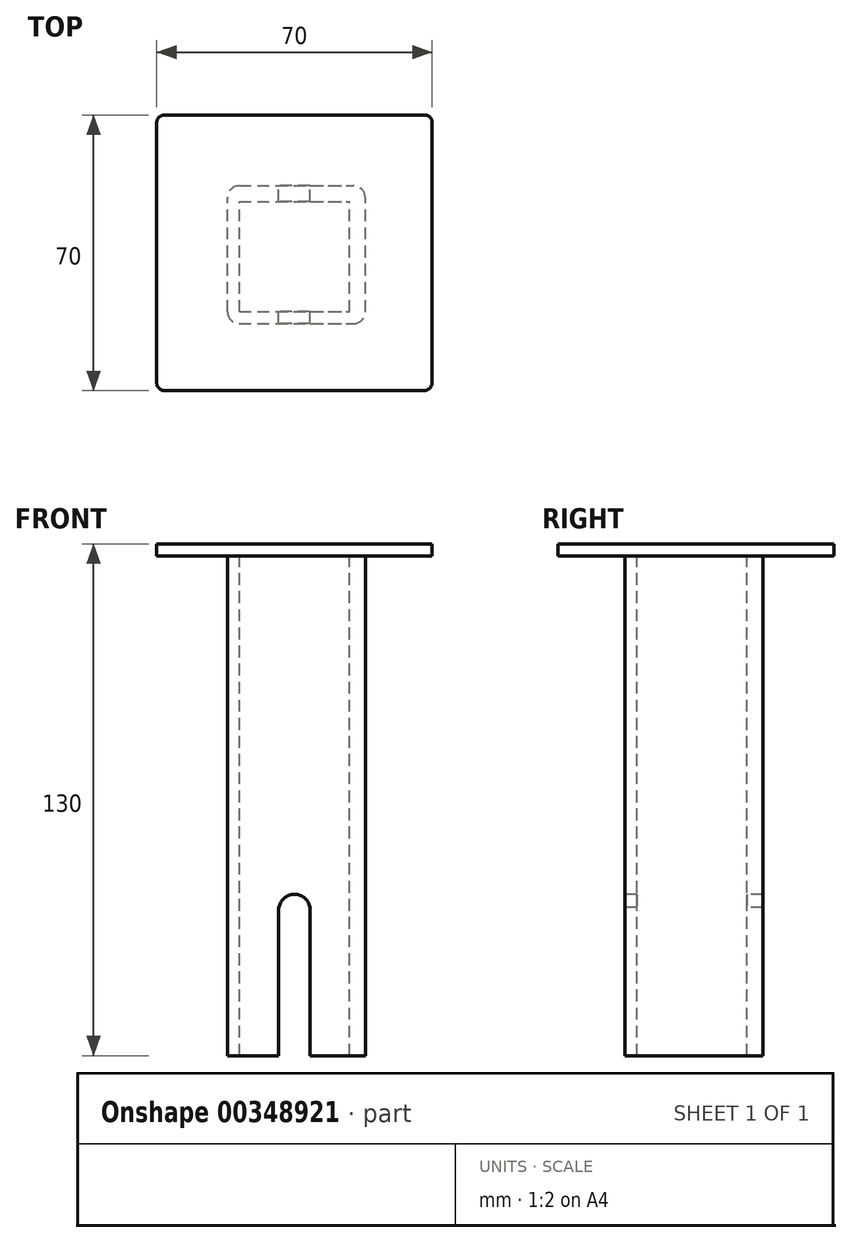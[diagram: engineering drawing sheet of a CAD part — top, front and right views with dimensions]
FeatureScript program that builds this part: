
annotation { "Feature Type Name" : "Feature", "Feature Type Description" : "" }
export const myFeature = defineFeature(function(context is Context, id is Id, definition is map)
    precondition{}
    {
        {
            var Q0;
            Q0=qCreatedBy(makeId("Top.planeOp"),FACE);
            var sketch = newSketch(context, id + "F0", { "sketchPlane" : qUnion([Q0])});
            skLineSegment(sketch, "E0.bottom", {"start": v(-35.5, -38.08) * mm, "end": v(34.5, -38.08) * mm});
            skLineSegment(sketch, "E0.top", {"start": v(-35.5, 31.92) * mm, "end": v(34.5, 31.92) * mm});
            skLineSegment(sketch, "E0.left", {"start": v(-35.5, -38.08) * mm, "end": v(-35.5, 31.92) * mm});
            skLineSegment(sketch, "E0.right", {"start": v(34.5, -38.08) * mm, "end": v(34.5, 31.92) * mm});
            skLineSegment(sketch, "E1", {"start": v(-35.5, -3.08) * mm, "end": v(-17.5, -3.08) * mm, "construction": true});
            skPoint(sketch, "E1.endSnap0", {"position": v(-35.5, -3.08) * mm});
            skLineSegment(sketch, "E2.bottom", {"start": v(-17.5, -21.08) * mm, "end": v(17.5, -21.08) * mm});
            skLineSegment(sketch, "E2.top", {"start": v(-17.5, 13.92) * mm, "end": v(17.5, 13.92) * mm});
            skLineSegment(sketch, "E2.left", {"start": v(-17.5, -21.08) * mm, "end": v(-17.5, 13.92) * mm});
            skLineSegment(sketch, "E2.right", {"start": v(17.5, -21.08) * mm, "end": v(17.5, 13.92) * mm});
            skLineSegment(sketch, "E3", {"start": v(-0.5, 31.92) * mm, "end": v(-0.5, 13.92) * mm, "construction": true});
            skPoint(sketch, "E3.endSnap0", {"position": v(0, 13.92) * mm});
            skLineSegment(sketch, "E4", {"start": v(-17.5, -3.08) * mm, "end": v(-14.5, -3.08) * mm, "construction": true});
            skLineSegment(sketch, "E5.bottom", {"start": v(-14.5, -18.08) * mm, "end": v(13.5, -18.08) * mm});
            skLineSegment(sketch, "E5.top", {"start": v(-14.5, 9.92) * mm, "end": v(13.5, 9.92) * mm});
            skLineSegment(sketch, "E5.left", {"start": v(-14.5, -18.08) * mm, "end": v(-14.5, 9.92) * mm});
            skLineSegment(sketch, "E5.right", {"start": v(13.5, -18.08) * mm, "end": v(13.5, 9.92) * mm});
            skLineSegment(sketch, "E6", {"start": v(0, -21.08) * mm, "end": v(0, -18.08) * mm, "construction": true});
            skLineSegment(sketch, "E7", {"start": v(-35.5, -38.08) * mm, "end": v(34.5, 31.92) * mm, "construction": true});
            skLineSegment(sketch, "E8", {"start": v(0, -21.08) * mm, "end": v(0, -38.08) * mm, "construction": true});
            skSolve(sketch);
        }
        {
            var Q0;
            {var subQ1=sQuery(id+"F0.wireOp",EDGE,"E0.bottom");Q0=makeQuery(id+"F0.imprint","IMPRINT",FACE,{"disambiguationData":[TD([[makeQuery(id+"F0.imprint","IMPRINT",EDGE,{"derivedFrom":subQ1}),1.0]])]});}
            var Q1;
            {var subQ7=sQuery(id+"F0.wireOp",EDGE,"E1");Q1=makeQuery(id+"F0.imprint","IMPRINT",FACE,{"disambiguationData":[TD([[makeQuery(id+"F0.imprint","IMPRINT",EDGE,{"derivedFrom":subQ7}),1.0]])]});}
            var Q2;
            {var subQ3=sQuery(id+"F0.wireOp",EDGE,"E5.bottom");Q2=makeQuery(id+"F0.imprint","IMPRINT",FACE,{"disambiguationData":[TD([[makeQuery(id+"F0.imprint","IMPRINT",EDGE,{"derivedFrom":subQ3}),1.0]])]});}
            var Q3;
            {var subQ9=sQuery(id+"F0.wireOp",EDGE,"E2.bottom");Q3=makeQuery(id+"F0.imprint","IMPRINT",FACE,{"disambiguationData":[TD([[makeQuery(id+"F0.imprint","IMPRINT",EDGE,{"derivedFrom":subQ9}),1.0]])]});}
            extrude(context, id + "F1", {"entities" : qUnion([Q0, Q1, Q2, Q3]), "oppositeDirection" : true, "depth" : 3 * mm});
        }
        {
            var Q0;
            {var subQ9=sQuery(id+"F0.wireOp",EDGE,"E2.bottom");Q0=makeQuery(id+"F0.imprint","IMPRINT",FACE,{"disambiguationData":[TD([[makeQuery(id+"F0.imprint","IMPRINT",EDGE,{"derivedFrom":subQ9}),1.0]])]});}
            extrude(context, id + "F2", {"entities" : qUnion([Q0]), "operationType" : NewBodyOperationType.ADD, "oppositeDirection" : true, "depth" : 130 * mm});
        }
        {
            var Q0;
            Q0=makeQuery(id+"F1.opExtrude","SWEPT_EDGE",EDGE,{"disambiguationData":[OSD([sQuery(id+"F0.wireOp",EDGE,"E0.bottom"),sQuery(id+"F0.wireOp",EDGE,"E0.left")])]});
            var Q1;
            Q1=makeQuery(id+"F1.opExtrude","SWEPT_EDGE",EDGE,{"disambiguationData":[OSD([sQuery(id+"F0.wireOp",EDGE,"E0.bottom"),sQuery(id+"F0.wireOp",EDGE,"E0.right")])]});
            var Q2;
            Q2=makeQuery(id+"F1.opExtrude","SWEPT_EDGE",EDGE,{"disambiguationData":[OSD([sQuery(id+"F0.wireOp",EDGE,"E0.top"),sQuery(id+"F0.wireOp",EDGE,"E0.left")])]});
            var Q3;
            Q3=makeQuery(id+"F1.opExtrude","SWEPT_EDGE",EDGE,{"disambiguationData":[OSD([sQuery(id+"F0.wireOp",EDGE,"E0.top"),sQuery(id+"F0.wireOp",EDGE,"E0.right")])]});
            fillet(context, id + "F3", {"entities" : qUnion([Q0, Q1, Q2, Q3]), "radius" : 2 * mm, "tangentPropagation" : true, "allowEdgeOverflow" : false});
        }
        {
            var Q0;
            Q0=makeQuery(id+"F2.opExtrude","SWEPT_FACE",FACE,{"disambiguationData":[OSD([sQuery(id+"F0.wireOp",EDGE,"E2.bottom")])]});
            var sketch = newSketch(context, id + "F4", { "sketchPlane" : qUnion([Q0])});
            skLineSegment(sketch, "E9", {"start": v(-17.5, -130) * mm, "end": v(-0.5, -130) * mm});
            skLineSegment(sketch, "E10", {"start": v(-0.5, -130) * mm, "end": v(-0.5, -167) * mm});
            skCircle(sketch, "E11", {"center": v(-0.5, -167) * mm, "radius": 4 * mm});
            skLineSegment(sketch, "E12", {"start": v(-4.5, -167) * mm, "end": v(-4.5, -130) * mm});
            skLineSegment(sketch, "E13", {"start": v(3.43, -167.72) * mm, "end": v(3.43, -130) * mm});
            skLineSegment(sketch, "E14", {"start": v(-17.5, -130) * mm, "end": v(17.5, -130) * mm});
            skLineSegment(sketch, "E15.MirrorCS", {"start": v(3.43, -92.28) * mm, "end": v(3.43, -130) * mm});
            skLineSegment(sketch, "E16.MirrorCS", {"start": v(-0.5, -130) * mm, "end": v(-0.5, -93) * mm});
            skLineSegment(sketch, "E17.MirrorCS", {"start": v(-4.5, -93) * mm, "end": v(-4.5, -130) * mm});
            skCircle(sketch, "E18.MirrorC", {"center": v(-0.5, -93) * mm, "radius": 4 * mm});
            skSolve(sketch);
        }
        {
            var Q0;
            {var subQ0=sQuery(id+"F4.wireOp",EDGE,"E10");var subQ3=sQuery(id+"F4.wireOp",EDGE,"E11");var subQ4=makeQuery(id+"F4.imprint","INTERSECT",VERTEX,{"derivedFrom":[subQ0,subQ3]});Q0=makeQuery(id+"F4.imprint","IMPRINT",FACE,{"disambiguationData":[TD([[makeQuery(id+"F4.imprint","IMPRINT",EDGE,{"disambiguationData":[TD([[subQ4,1.0]])],"derivedFrom":subQ3}),-1.0]])]});}
            var Q1;
            {var subQ0=sQuery(id+"F4.wireOp",EDGE,"E11");var subQ1=makeQuery(id+"F4.imprint","INTERSECT",VERTEX,{"derivedFrom":[sQuery(id+"F4.wireOp",EDGE,"E10"),subQ0]});Q1=makeQuery(id+"F4.imprint","IMPRINT",FACE,{"disambiguationData":[TD([[makeQuery(id+"F4.imprint","IMPRINT",EDGE,{"disambiguationData":[TD([[subQ1,1.0]])],"derivedFrom":subQ0}),1.0]])]});}
            var Q2;
            {var subQ3=sQuery(id+"F4.wireOp",EDGE,"E12");Q2=makeQuery(id+"F4.imprint","IMPRINT",FACE,{"disambiguationData":[TD([[makeQuery(id+"F4.imprint","IMPRINT",EDGE,{"derivedFrom":subQ3}),-1.0]])]});}
            var Q3;
            {var subQ3=sQuery(id+"F4.wireOp",EDGE,"E17.MirrorCS");Q3=makeQuery(id+"F4.imprint","IMPRINT",FACE,{"disambiguationData":[TD([[makeQuery(id+"F4.imprint","IMPRINT",EDGE,{"derivedFrom":subQ3}),1.0]])]});}
            var Q4;
            {var subQ0=sQuery(id+"F4.wireOp",EDGE,"E16.MirrorCS");var subQ5=sQuery(id+"F4.wireOp",EDGE,"E18.MirrorC");var subQ7=makeQuery(id+"F4.imprint","INTERSECT",VERTEX,{"derivedFrom":[subQ0,subQ5]});Q4=makeQuery(id+"F4.imprint","IMPRINT",FACE,{"disambiguationData":[TD([[makeQuery(id+"F4.imprint","IMPRINT",EDGE,{"disambiguationData":[TD([[subQ7,1.0]])],"derivedFrom":subQ5}),1.0]])]});}
            var Q5;
            {var subQ0=sQuery(id+"F4.wireOp",EDGE,"E18.MirrorC");var subQ1=sQuery(id+"F4.wireOp",EDGE,"E15.MirrorCS");var subQ2=makeQuery(id+"F4.imprint","INTERSECT",VERTEX,{"disambiguationData":[OD(0.0)],"derivedFrom":[subQ1,subQ0]});Q5=makeQuery(id+"F4.imprint","IMPRINT",FACE,{"disambiguationData":[TD([[makeQuery(id+"F4.imprint","IMPRINT",EDGE,{"disambiguationData":[TD([[subQ2,-1.0]])],"derivedFrom":subQ1}),-1.0]])]});}
            extrude(context, id + "F5", {"entities" : qUnion([Q0, Q1, Q2, Q3, Q4, Q5]), "operationType" : NewBodyOperationType.REMOVE, "oppositeDirection" : true, "depth" : 35 * mm});
        }
        {
            var Q0;
            Q0=makeQuery(id+"F2.opExtrude","SWEPT_EDGE",EDGE,{"disambiguationData":[OSD([sQuery(id+"F0.wireOp",EDGE,"E2.bottom"),sQuery(id+"F0.wireOp",EDGE,"E2.right")])]});
            var Q1;
            Q1=makeQuery(id+"F2.opExtrude","SWEPT_EDGE",EDGE,{"disambiguationData":[OSD([sQuery(id+"F0.wireOp",EDGE,"E2.top"),sQuery(id+"F0.wireOp",EDGE,"E2.right")])]});
            var Q2;
            Q2=makeQuery(id+"F2.opExtrude","SWEPT_EDGE",EDGE,{"disambiguationData":[OSD([sQuery(id+"F0.wireOp",EDGE,"E2.bottom"),sQuery(id+"F0.wireOp",EDGE,"E2.left")])]});
            var Q3;
            Q3=makeQuery(id+"F2.opExtrude","SWEPT_EDGE",EDGE,{"disambiguationData":[OSD([sQuery(id+"F0.wireOp",EDGE,"E2.top"),sQuery(id+"F0.wireOp",EDGE,"E2.left")])]});
            fillet(context, id + "F6", {"entities" : qUnion([Q0, Q1, Q2, Q3]), "radius" : 3 * mm, "tangentPropagation" : true, "allowEdgeOverflow" : false});
        }
    });
